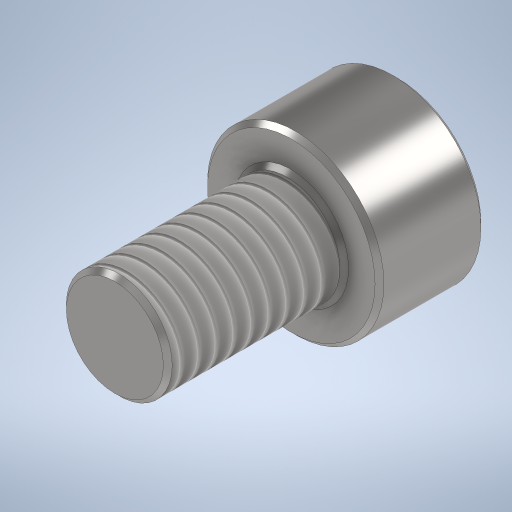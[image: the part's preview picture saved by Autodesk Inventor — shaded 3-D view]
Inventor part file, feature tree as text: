
AUTODESK INVENTOR PART (.ipt)
format: ipt  version: 2024 (Build 280153000, 153)  size: 325,120 bytes
history: native  units: mm
features: extrude x3, chamfer x3, sketch x2, thread x1, hole x1
ambient origin geometry x8: Origin, YZ Plane, XZ Plane, XY Plane, X Axis, Y Axis, Z Axis, Center Point
bodies: Solid1 (feature_tree)
feature tree (10):
  sketch  "Sketch1"  dims[d0=10.0mm d1=6.0mm]
  extrude  "Extrusion1"  Depth=10.0mm
  extrude  "Extrusion2"  Depth=3.0mm TaperAngle=0.0deg
  thread  "Thread1"  [1 undecoded]
  chamfer  "Chamfer1"  Distance=5.0mm
  sketch  "Sketch2"  dims[d2=10.0mm d3=0.0mm d4=6.0mm d5=0.0mm d6=8.0mm d7=0.0mm d8=0.25mm d9=2.0mm d10=45.0deg d11=4.5mm d12=5.0mm d15=0.75mm d16=2.0mm d17=45.0deg d18=3.0mm d19=0.0mm d20=0.25mm d21=2.0mm d22=45.0deg d23=4.5mm d24=6.0mm d25=4.0mm d26=2.0mm d27=90.0deg d28=3.0mm d29=150.0deg]
  hole  "Hole1"  [1 undecoded]
  chamfer  "Chamfer2"  Distance=3.0mm
  extrude  "Extrusion4"  Depth=3.0mm TaperAngle=45.0deg
  chamfer  "Chamfer3"  Distance=4.5mm
note: 2 required parameter values undecoded (feature->parameter linkage not recoverable at this tier; creation-order binding heuristic only, values carry confidence <= 0.55)
